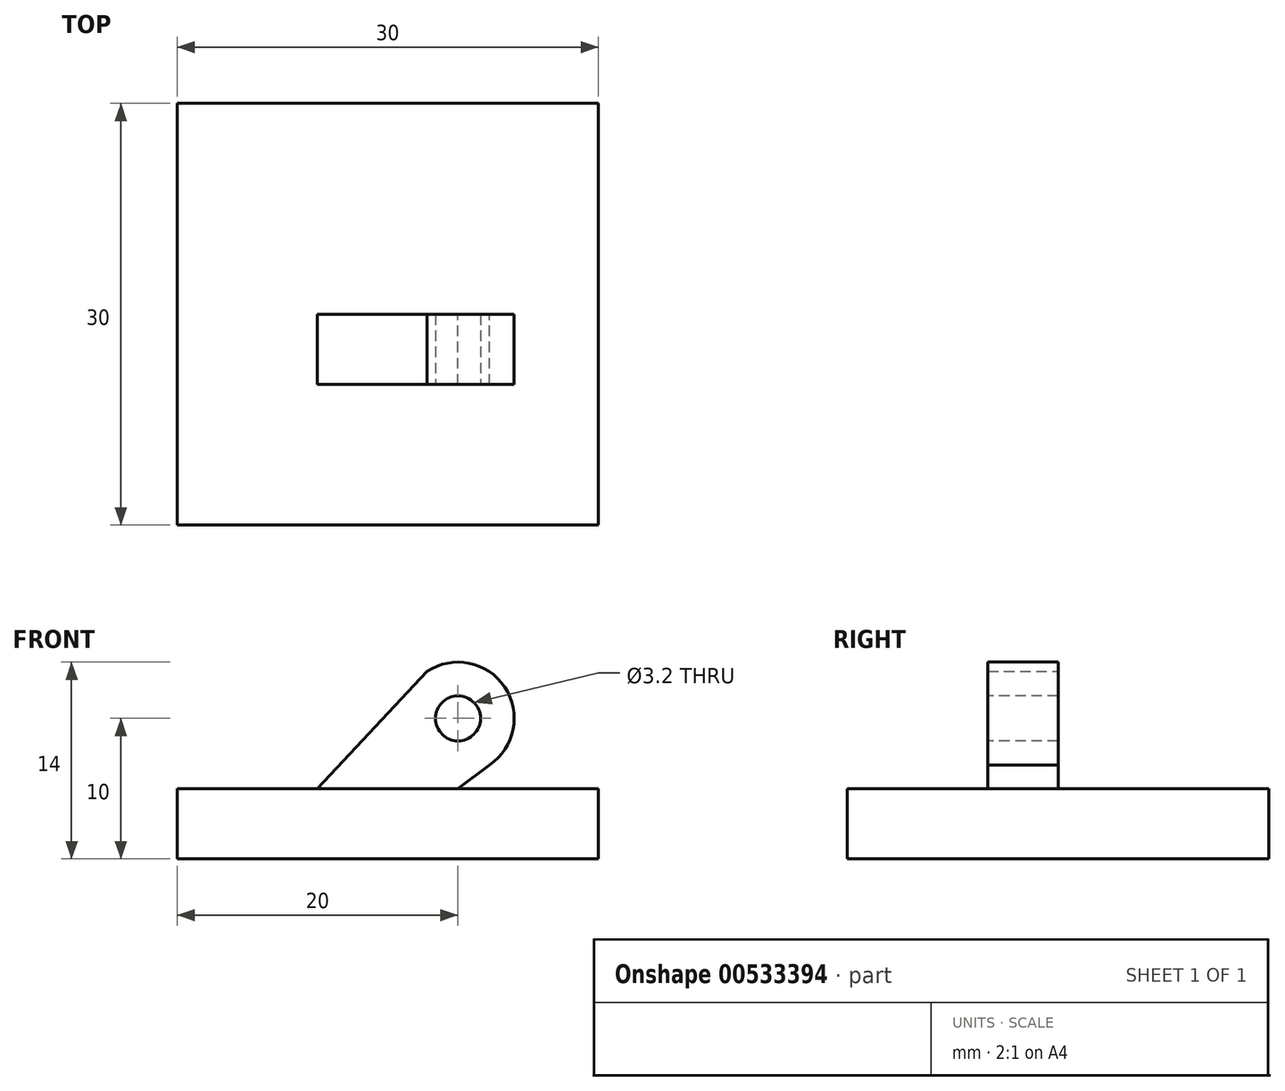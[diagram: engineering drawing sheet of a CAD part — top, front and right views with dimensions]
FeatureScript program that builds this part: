
annotation { "Feature Type Name" : "Feature", "Feature Type Description" : "" }
export const myFeature = defineFeature(function(context is Context, id is Id, definition is map)
    precondition{}
    {
        {
            var Q0;
            Q0=qCreatedBy(makeId("Top.planeOp"),FACE);
            var sketch = newSketch(context, id + "F0", { "sketchPlane" : qUnion([Q0])});
            skLineSegment(sketch, "E0.bottom", {"start": v(15, -15) * mm, "end": v(-15, -15) * mm});
            skLineSegment(sketch, "E0.top", {"start": v(15, 15) * mm, "end": v(-15, 15) * mm});
            skLineSegment(sketch, "E0.left", {"start": v(15, -15) * mm, "end": v(15, 15) * mm});
            skLineSegment(sketch, "E0.right", {"start": v(-15, -15) * mm, "end": v(-15, 15) * mm});
            skPoint(sketch, "E0.middle", {"position": v(0, 0) * mm});
            skSolve(sketch);
        }
        {
            var Q0;
            Q0 = qSketchRegion(id + "F0", true);
            extrude(context, id + "F1", {"entities" : qUnion([Q0]), "depth" : 5 * mm, "offsetDistance" : 25 * mm});
        }
        {
            var Q0;
            Q0=qCreatedBy(makeId("Front.planeOp"),FACE);
            var sketch = newSketch(context, id + "F2", { "sketchPlane" : qUnion([Q0])});
            skLineSegment(sketch, "E1", {"start": v(0, 0) * mm, "end": v(0, 5) * mm});
            skLineSegment(sketch, "E2.bottom", {"start": v(0, 5) * mm, "end": v(5, 5) * mm});
            skLineSegment(sketch, "E2.top", {"start": v(0, 10) * mm, "end": v(5, 10) * mm});
            skLineSegment(sketch, "E2.left", {"start": v(0, 5) * mm, "end": v(0, 10) * mm});
            skLineSegment(sketch, "E2.right", {"start": v(5, 5) * mm, "end": v(5, 10) * mm});
            skCircle(sketch, "E3", {"center": v(5, 10) * mm, "radius": 4 * mm});
            skLineSegment(sketch, "E4", {"start": v(5, 5) * mm, "end": v(-3.15, 5) * mm});
            skLineSegment(sketch, "E5", {"start": v(7.24, 6.69) * mm, "end": v(2.79, 13.33) * mm});
            skLineSegment(sketch, "E6", {"start": v(7.24, 6.69) * mm, "end": v(5, 5) * mm});
            skLineSegment(sketch, "E7", {"start": v(5, 5) * mm, "end": v(-5, 5) * mm});
            skLineSegment(sketch, "E8", {"start": v(2.79, 13.33) * mm, "end": v(-5, 5) * mm});
            skSolve(sketch);
        }
        {
            var Q0;
            {var subQ0=sQuery(id+"F2.wireOp",EDGE,"E5");Q0=makeQuery(id+"F2.imprint","IMPRINT",FACE,{"disambiguationData":[TD([[makeQuery(id+"F2.imprint","IMPRINT",EDGE,{"derivedFrom":subQ0}),-1.0]])]});}
            var Q1;
            {var subQ0=sQuery(id+"F2.wireOp",EDGE,"E5");Q1=makeQuery(id+"F2.imprint","IMPRINT",FACE,{"disambiguationData":[TD([[makeQuery(id+"F2.imprint","IMPRINT",EDGE,{"derivedFrom":subQ0}),1.0]])]});}
            var Q2;
            {var subQ0=sQuery(id+"F2.wireOp",EDGE,"E2.right");var subQ1=sQuery(id+"F2.wireOp",EDGE,"E2.top");var subQ2=makeQuery(id+"F2.imprint","INTERSECT",VERTEX,{"derivedFrom":[subQ1,subQ0]});Q2=makeQuery(id+"F2.imprint","IMPRINT",FACE,{"disambiguationData":[TD([[makeQuery(id+"F2.imprint","IMPRINT",EDGE,{"disambiguationData":[TD([[subQ2,1.0]])],"derivedFrom":subQ1}),-1.0]])]});}
            var Q3;
            {var subQ1=sQuery(id+"F2.wireOp",EDGE,"E2.left");Q3=makeQuery(id+"F2.imprint","IMPRINT",FACE,{"disambiguationData":[TD([[makeQuery(id+"F2.imprint","IMPRINT",EDGE,{"derivedFrom":subQ1}),1.0]])]});}
            var Q4;
            {var subQ7=sQuery(id+"F2.wireOp",EDGE,"E2.left");Q4=makeQuery(id+"F2.imprint","IMPRINT",FACE,{"disambiguationData":[TD([[makeQuery(id+"F2.imprint","IMPRINT",EDGE,{"derivedFrom":subQ7}),-1.0]])]});}
            var Q5;
            {var subQ0=sQuery(id+"F2.wireOp",EDGE,"E6");Q5=makeQuery(id+"F2.imprint","IMPRINT",FACE,{"disambiguationData":[TD([[makeQuery(id+"F2.imprint","IMPRINT",EDGE,{"derivedFrom":subQ0}),-1.0]])]});}
            extrude(context, id + "F3", {"entities" : qUnion([Q0, Q1, Q2, Q3, Q4, Q5]), "operationType" : NewBodyOperationType.ADD, "depth" : 5 * mm, "offsetDistance" : 25 * mm});
        }
        {
            var Q0;
            Q0=makeQuery(id+"F3.opExtrude","CAP_FACE",FACE,{"disambiguationData":[OSD([sQuery(id+"F2.wireOp",EDGE,"E3"),sQuery(id+"F2.wireOp",EDGE,"E6"),sQuery(id+"F2.wireOp",EDGE,"E7"),sQuery(id+"F2.wireOp",EDGE,"E8")])],"isStart":false});
            var sketch = newSketch(context, id + "F4", { "sketchPlane" : qUnion([Q0])});
            skCircle(sketch, "E9", {"center": v(5, 10) * mm, "radius": 1.6 * mm});
            skSolve(sketch);
        }
        {
            var Q0;
            Q0=makeQuery(id+"F4.imprint","IMPRINT",FACE,{"disambiguationData":[TD([[makeQuery(id+"F4.imprint","IMPRINT",EDGE,{"derivedFrom":sQuery(id+"F4.wireOp",EDGE,"E9")}),1.0]])]});
            extrude(context, id + "F5", {"entities" : qUnion([Q0]), "operationType" : NewBodyOperationType.REMOVE, "endBound" : BoundingType.THROUGH_ALL, "oppositeDirection" : true, "depth" : 25 * mm, "offsetDistance" : 25 * mm});
        }
    });
